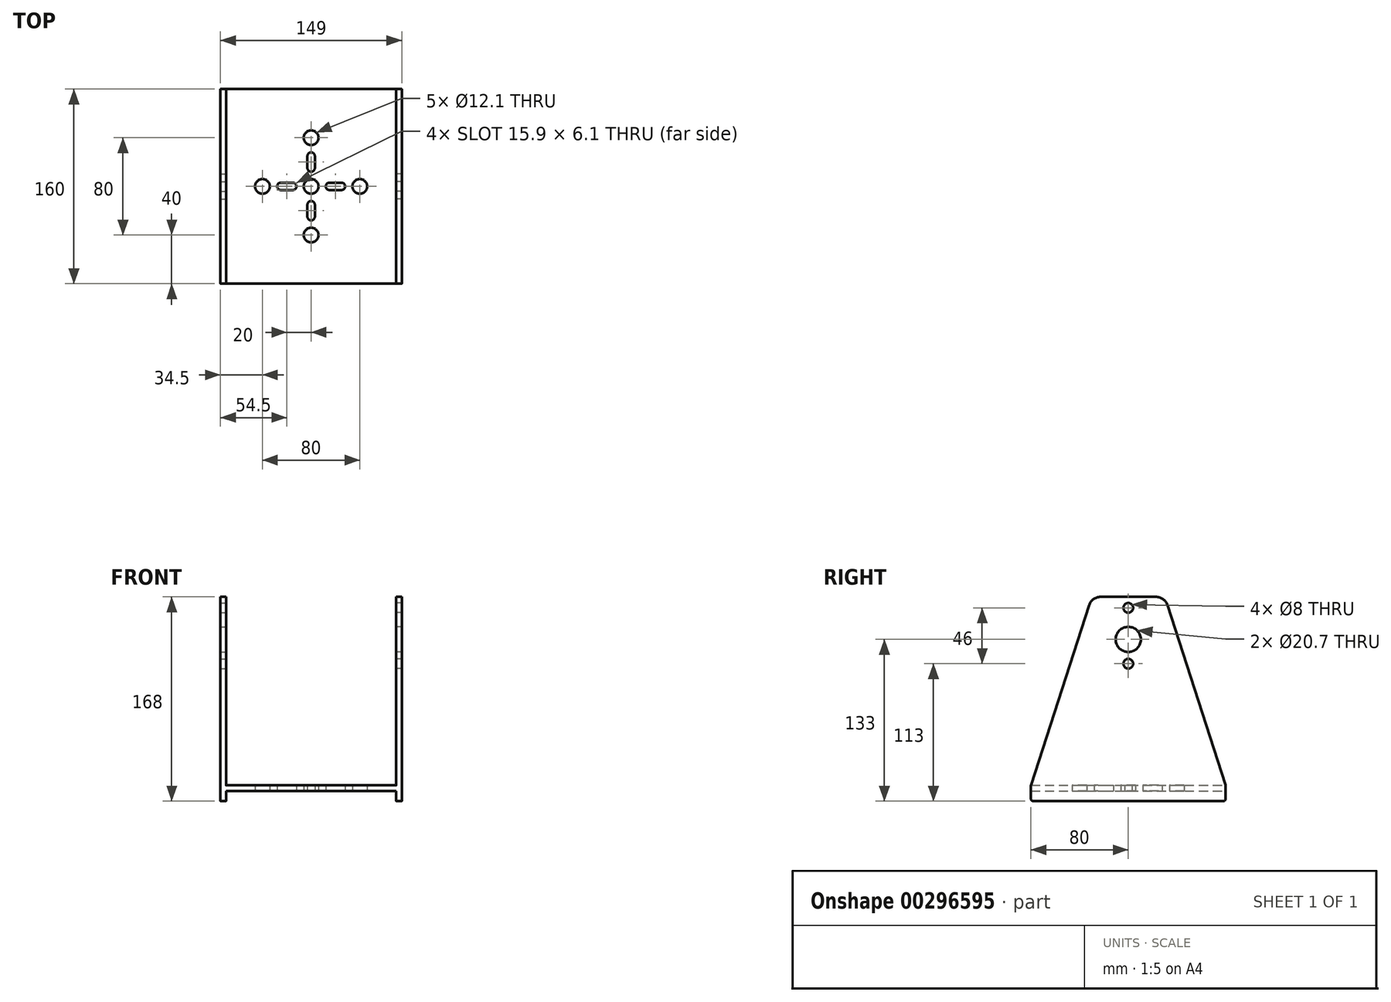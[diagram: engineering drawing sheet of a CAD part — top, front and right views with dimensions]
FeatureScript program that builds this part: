
annotation { "Feature Type Name" : "Feature", "Feature Type Description" : "" }
export const myFeature = defineFeature(function(context is Context, id is Id, definition is map)
    precondition{}
    {
        {
            var Q0;
            Q0=qCreatedBy(makeId("Top.planeOp"),FACE);
            var sketch = newSketch(context, id + "F0", { "sketchPlane" : qUnion([Q0])});
            skLineSegment(sketch, "E0.bottom", {"start": v(70, -80) * mm, "end": v(-70, -80) * mm});
            skLineSegment(sketch, "E0.top", {"start": v(70, 80) * mm, "end": v(-70, 80) * mm});
            skLineSegment(sketch, "E0.left", {"start": v(70, -80) * mm, "end": v(70, 80) * mm});
            skLineSegment(sketch, "E0.right", {"start": v(-70, -80) * mm, "end": v(-70, 80) * mm});
            skPoint(sketch, "E0.middle", {"position": v(0, 0) * mm});
            skLineSegment(sketch, "E1", {"start": v(0, 80) * mm, "end": v(0, -80) * mm, "construction": true});
            skLineSegment(sketch, "E2", {"start": v(-70, 0) * mm, "end": v(70, 0) * mm, "construction": true});
            skCircle(sketch, "E3", {"center": v(0, 0) * mm, "radius": 6.05 * mm});
            skCircle(sketch, "E4", {"center": v(-40, 0) * mm, "radius": 6.05 * mm});
            skCircle(sketch, "E5", {"center": v(0, 40) * mm, "radius": 6.05 * mm});
            skCircle(sketch, "E6", {"center": v(40, 0) * mm, "radius": 6.05 * mm});
            skCircle(sketch, "E7", {"center": v(0, -40) * mm, "radius": 6.05 * mm});
            skArc(sketch, "E8", {"start": v(3.05, 24.9) * mm, "mid": v(0, 27.95) * mm, "end": v(-3.05, 24.9) * mm});
            skArc(sketch, "E9", {"start": v(-3.05, 15.1) * mm, "mid": v(0, 12.05) * mm, "end": v(3.05, 15.1) * mm});
            skLineSegment(sketch, "E10", {"start": v(-3.05, 24.9) * mm, "end": v(-3.05, 15.1) * mm});
            skLineSegment(sketch, "E11", {"start": v(3.05, 24.9) * mm, "end": v(3.05, 15.1) * mm});
            skLineSegment(sketch, "E12.1.0", {"start": v(-24.9, 3.05) * mm, "end": v(-15.1, 3.05) * mm});
            skArc(sketch, "E12.1.1", {"start": v(-15.1, -3.05) * mm, "mid": v(-12.05, 0) * mm, "end": v(-15.1, 3.05) * mm});
            skLineSegment(sketch, "E12.1.2", {"start": v(-24.9, -3.05) * mm, "end": v(-15.1, -3.05) * mm});
            skArc(sketch, "E12.1.3", {"start": v(-24.9, 3.05) * mm, "mid": v(-27.95, 0) * mm, "end": v(-24.9, -3.05) * mm});
            skLineSegment(sketch, "E12.2.0", {"start": v(-3.05, -24.9) * mm, "end": v(-3.05, -15.1) * mm});
            skArc(sketch, "E12.2.1", {"start": v(3.05, -15.1) * mm, "mid": v(0, -12.05) * mm, "end": v(-3.05, -15.1) * mm});
            skLineSegment(sketch, "E12.2.2", {"start": v(3.05, -24.9) * mm, "end": v(3.05, -15.1) * mm});
            skArc(sketch, "E12.2.3", {"start": v(-3.05, -24.9) * mm, "mid": v(0, -27.95) * mm, "end": v(3.05, -24.9) * mm});
            skLineSegment(sketch, "E12.3.0", {"start": v(24.9, -3.05) * mm, "end": v(15.1, -3.05) * mm});
            skArc(sketch, "E12.3.1", {"start": v(15.1, 3.05) * mm, "mid": v(12.05, 0) * mm, "end": v(15.1, -3.05) * mm});
            skLineSegment(sketch, "E12.3.2", {"start": v(24.9, 3.05) * mm, "end": v(15.1, 3.05) * mm});
            skArc(sketch, "E12.3.3", {"start": v(24.9, -3.05) * mm, "mid": v(27.95, 0) * mm, "end": v(24.9, 3.05) * mm});
            skSolve(sketch);
        }
        {
            var Q0;
            Q0 = qSketchRegion(id + "F0", true);
            extrude(context, id + "F1", {"entities" : qUnion([Q0]), "depth" : 4.5 * mm});
        }
        {
            var Q0;
            Q0=makeQuery(id+"F1.opExtrude","SWEPT_FACE",FACE,{"disambiguationData":[OSD([sQuery(id+"F0.wireOp",EDGE,"E0.left")])]});
            var sketch = newSketch(context, id + "F2", { "sketchPlane" : qUnion([Q0])});
            skLineSegment(sketch, "E13", {"start": v(0, 4.5) * mm, "end": v(0, 159.5) * mm, "construction": true});
            skPoint(sketch, "E13.endSnap0", {"position": v(0, 4.5) * mm});
            skLineSegment(sketch, "E14", {"start": v(-22.72, 159.5) * mm, "end": v(22.72, 159.5) * mm});
            skLineSegment(sketch, "E15", {"start": v(-32.24, 152.57) * mm, "end": v(-79.9, 4.8) * mm});
            skLineSegment(sketch, "E16", {"start": v(-80, 4.19) * mm, "end": v(-80, -6.5) * mm});
            skLineSegment(sketch, "E17", {"start": v(-78, -8.5) * mm, "end": v(78, -8.5) * mm});
            skLineSegment(sketch, "E18", {"start": v(80, -6.5) * mm, "end": v(80, 4.19) * mm});
            skLineSegment(sketch, "E19", {"start": v(79.9, 4.8) * mm, "end": v(32.24, 152.57) * mm});
            skCircle(sketch, "E20", {"center": v(0, 124.5) * mm, "radius": 10.35 * mm});
            skCircle(sketch, "E21", {"center": v(0, 150.5) * mm, "radius": 4 * mm});
            skCircle(sketch, "E22", {"center": v(0, 104.5) * mm, "radius": 4 * mm});
            skPoint(sketch, "E23.visualSharp", {"position": v(-30, 159.5) * mm});
            skArc(sketch, "E23.filletArc", {"start": v(-22.72, 159.5) * mm, "mid": v(-28.6, 157.58) * mm, "end": v(-32.24, 152.57) * mm});
            skPoint(sketch, "E24.visualSharp", {"position": v(30, 159.5) * mm});
            skArc(sketch, "E24.filletArc", {"start": v(32.24, 152.57) * mm, "mid": v(28.6, 157.58) * mm, "end": v(22.72, 159.5) * mm});
            skPoint(sketch, "E25.visualSharp", {"position": v(-80, -8.5) * mm});
            skArc(sketch, "E25.filletArc", {"start": v(-80, -6.5) * mm, "mid": v(-79.41, -7.91) * mm, "end": v(-78, -8.5) * mm});
            skPoint(sketch, "E26.visualSharp", {"position": v(80, -8.5) * mm});
            skArc(sketch, "E26.filletArc", {"start": v(78, -8.5) * mm, "mid": v(79.41, -7.91) * mm, "end": v(80, -6.5) * mm});
            skPoint(sketch, "E27.visualSharp", {"position": v(80, 4.5) * mm});
            skArc(sketch, "E27.filletArc", {"start": v(80, 4.19) * mm, "mid": v(79.98, 4.5) * mm, "end": v(79.9, 4.8) * mm});
            skPoint(sketch, "E28.visualSharp", {"position": v(-80, 4.5) * mm});
            skArc(sketch, "E28.filletArc", {"start": v(-79.9, 4.8) * mm, "mid": v(-79.98, 4.5) * mm, "end": v(-80, 4.19) * mm});
            skSolve(sketch);
        }
        {
            var Q0;
            Q0 = qSketchRegion(id + "F2", true);
            extrude(context, id + "F3", {"entities" : qUnion([Q0]), "depth" : 4.5 * mm});
        }
        {
            var Q0;
            Q0=makeQuery(id+"F3.opExtrude","SWEPT_BODY",BODY,{"disambiguationData":[OSD([sQuery(id+"F2.wireOp",EDGE,"E14"),sQuery(id+"F2.wireOp",EDGE,"E15"),sQuery(id+"F2.wireOp",EDGE,"E16"),sQuery(id+"F2.wireOp",EDGE,"E17"),sQuery(id+"F2.wireOp",EDGE,"E18"),sQuery(id+"F2.wireOp",EDGE,"E19"),sQuery(id+"F2.wireOp",EDGE,"E20"),sQuery(id+"F2.wireOp",EDGE,"E21"),sQuery(id+"F2.wireOp",EDGE,"E22"),sQuery(id+"F2.wireOp",EDGE,"E23.filletArc"),sQuery(id+"F2.wireOp",EDGE,"E24.filletArc"),sQuery(id+"F2.wireOp",EDGE,"E25.filletArc"),sQuery(id+"F2.wireOp",EDGE,"E26.filletArc"),sQuery(id+"F2.wireOp",EDGE,"E27.filletArc"),sQuery(id+"F2.wireOp",EDGE,"E28.filletArc")])]});
            var Q1;
            Q1=qCreatedBy(makeId("Right.planeOp"),FACE);
            mirror(context, id + "F4", {"operationType" : NewBodyOperationType.ADD, "entities" : qUnion([Q0]), "mirrorPlane" : qUnion([Q1])});
        }
    });
